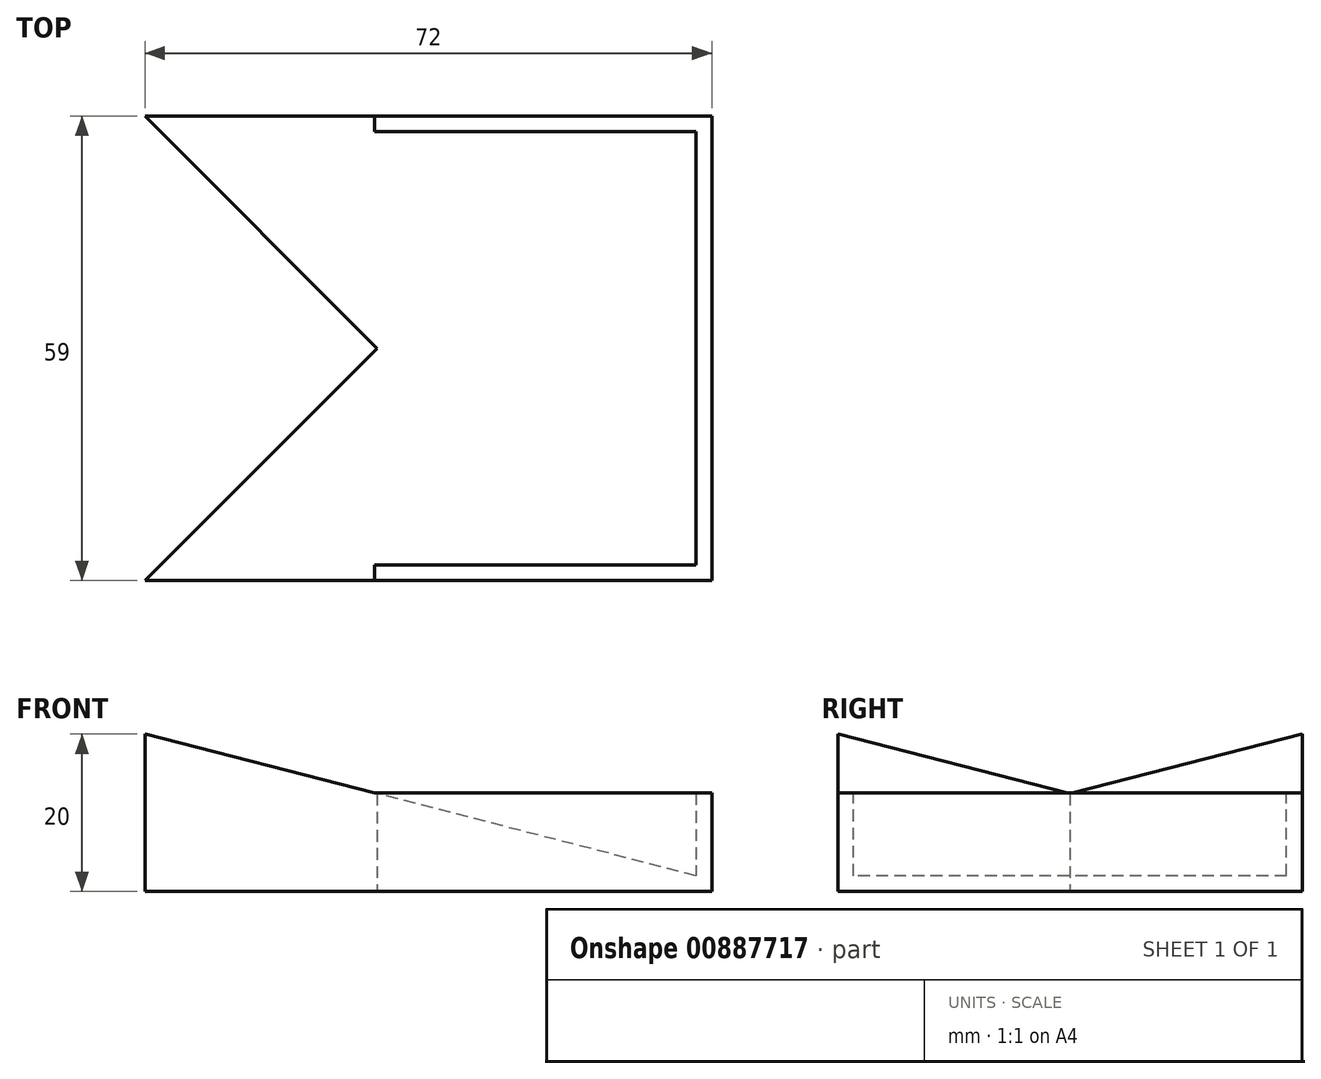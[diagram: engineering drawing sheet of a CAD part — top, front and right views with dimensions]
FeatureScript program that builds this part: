
annotation { "Feature Type Name" : "Feature", "Feature Type Description" : "" }
export const myFeature = defineFeature(function(context is Context, id is Id, definition is map)
    precondition{}
    {
        {
            var Q0;
            Q0=qCreatedBy(makeId("Front.planeOp"),FACE);
            cPlane(context, id + "F0", {"entities" : qUnion([Q0]), "cplaneType" : CPlaneType.OFFSET, "offset" : 59 * mm, "width" : 150 * mm, "height" : 150 * mm});
        }
        {
            var Q0;
            Q0=qCreatedBy(makeId("Right.planeOp"),FACE);
            cPlane(context, id + "F1", {"entities" : qUnion([Q0]), "cplaneType" : CPlaneType.OFFSET, "offset" : 72 * mm, "width" : 150 * mm, "height" : 150 * mm});
        }
        {
            var Q0;
            Q0=qCreatedBy(id+"F0.planeOp",FACE);
            var sketch = newSketch(context, id + "F2", { "sketchPlane" : qUnion([Q0])});
            skLineSegment(sketch, "E0", {"start": v(0, 0) * mm, "end": v(0, 20) * mm});
            skLineSegment(sketch, "E1", {"start": v(0, 20) * mm, "end": v(70, 2) * mm});
            skLineSegment(sketch, "E2", {"start": v(70, 2) * mm, "end": v(70, 0) * mm});
            skLineSegment(sketch, "E3", {"start": v(70, 0) * mm, "end": v(0, 0) * mm});
            skSolve(sketch);
        }
        {
            var Q0;
            Q0=makeQuery(id+"F2.imprint","IMPRINT",FACE,{"disambiguationData":[TD([[makeQuery(id+"F2.imprint","IMPRINT",EDGE,{"derivedFrom":sQuery(id+"F2.wireOp",EDGE,"E0")}),-1.0]])]});
            extrude(context, id + "F3", {"entities" : qUnion([Q0]), "oppositeDirection" : true, "depth" : 59 * mm, "offsetDistance" : 25 * mm});
        }
        {
            var Q0;
            Q0=qCreatedBy(id+"F1.planeOp",FACE);
            var sketch = newSketch(context, id + "F4", { "sketchPlane" : qUnion([Q0])});
            skLineSegment(sketch, "E4.bottom", {"start": v(0, 0) * mm, "end": v(-59, 0) * mm});
            skLineSegment(sketch, "E4.top", {"start": v(0, 12.5) * mm, "end": v(-59, 12.5) * mm});
            skLineSegment(sketch, "E4.left", {"start": v(0, 0) * mm, "end": v(0, 12.5) * mm});
            skLineSegment(sketch, "E4.right", {"start": v(-59, 0) * mm, "end": v(-59, 12.5) * mm});
            skSolve(sketch);
        }
        {
            var Q0;
            Q0=makeQuery(id+"F4.imprint","IMPRINT",FACE,{"disambiguationData":[TD([[makeQuery(id+"F4.imprint","IMPRINT",EDGE,{"derivedFrom":sQuery(id+"F4.wireOp",EDGE,"E4.bottom")}),-1.0]])]});
            extrude(context, id + "F5", {"entities" : qUnion([Q0]), "operationType" : NewBodyOperationType.ADD, "oppositeDirection" : true, "depth" : 2 * mm, "offsetDistance" : 25 * mm});
        }
        {
            var Q0;
            Q0=qCreatedBy(makeId("Front.planeOp"),FACE);
            var sketch = newSketch(context, id + "F6", { "sketchPlane" : qUnion([Q0])});
            skLineSegment(sketch, "E5.bottom", {"start": v(71.6, 0) * mm, "end": v(6.6, 0) * mm});
            skLineSegment(sketch, "E5.top", {"start": v(71.6, 12.5) * mm, "end": v(6.6, 12.5) * mm});
            skLineSegment(sketch, "E5.left", {"start": v(71.6, 0) * mm, "end": v(71.6, 12.5) * mm});
            skLineSegment(sketch, "E5.right", {"start": v(6.6, 0) * mm, "end": v(6.6, 12.5) * mm});
            skSolve(sketch);
        }
        {
            var Q0;
            Q0=makeQuery(id+"F6.imprint","IMPRINT",FACE,{"disambiguationData":[TD([[makeQuery(id+"F6.imprint","IMPRINT",EDGE,{"derivedFrom":sQuery(id+"F6.wireOp",EDGE,"E5.bottom")}),-1.0]])]});
            extrude(context, id + "F7", {"entities" : qUnion([Q0]), "operationType" : NewBodyOperationType.ADD, "depth" : 2 * mm, "offsetDistance" : 25 * mm});
        }
        {
            var Q0;
            Q0=qCreatedBy(id+"F0.planeOp",FACE);
            var sketch = newSketch(context, id + "F8", { "sketchPlane" : qUnion([Q0])});
            skLineSegment(sketch, "E6.bottom", {"start": v(71.76, 0) * mm, "end": v(6.76, 0) * mm});
            skLineSegment(sketch, "E6.top", {"start": v(71.76, 12.5) * mm, "end": v(6.76, 12.5) * mm});
            skLineSegment(sketch, "E6.left", {"start": v(71.76, 0) * mm, "end": v(71.76, 12.5) * mm});
            skLineSegment(sketch, "E6.right", {"start": v(6.76, 0) * mm, "end": v(6.76, 12.5) * mm});
            skSolve(sketch);
        }
        {
            var Q0;
            Q0=makeQuery(id+"F8.imprint","IMPRINT",FACE,{"disambiguationData":[TD([[makeQuery(id+"F8.imprint","IMPRINT",EDGE,{"derivedFrom":sQuery(id+"F8.wireOp",EDGE,"E6.bottom")}),-1.0]])]});
            extrude(context, id + "F9", {"entities" : qUnion([Q0]), "operationType" : NewBodyOperationType.ADD, "oppositeDirection" : true, "depth" : 2 * mm, "offsetDistance" : 25 * mm});
        }
        {
            var Q0;
            Q0=qCreatedBy(makeId("Top.planeOp"),FACE);
            var sketch = newSketch(context, id + "F10", { "sketchPlane" : qUnion([Q0])});
            skLineSegment(sketch, "E7", {"start": v(0, 0) * mm, "end": v(0, -59) * mm});
            skLineSegment(sketch, "E8", {"start": v(0, -59) * mm, "end": v(29.5, -29.5) * mm});
            skLineSegment(sketch, "E9", {"start": v(29.5, -29.5) * mm, "end": v(0, 0) * mm});
            skSolve(sketch);
        }
        {
            var Q0;
            Q0=makeQuery(id+"F10.imprint","IMPRINT",FACE,{"disambiguationData":[TD([[makeQuery(id+"F10.imprint","IMPRINT",EDGE,{"derivedFrom":sQuery(id+"F10.wireOp",EDGE,"E7")}),1.0]])]});
            extrude(context, id + "F11", {"entities" : qUnion([Q0]), "operationType" : NewBodyOperationType.REMOVE, "depth" : 25 * mm, "offsetDistance" : 25 * mm});
        }
    });
